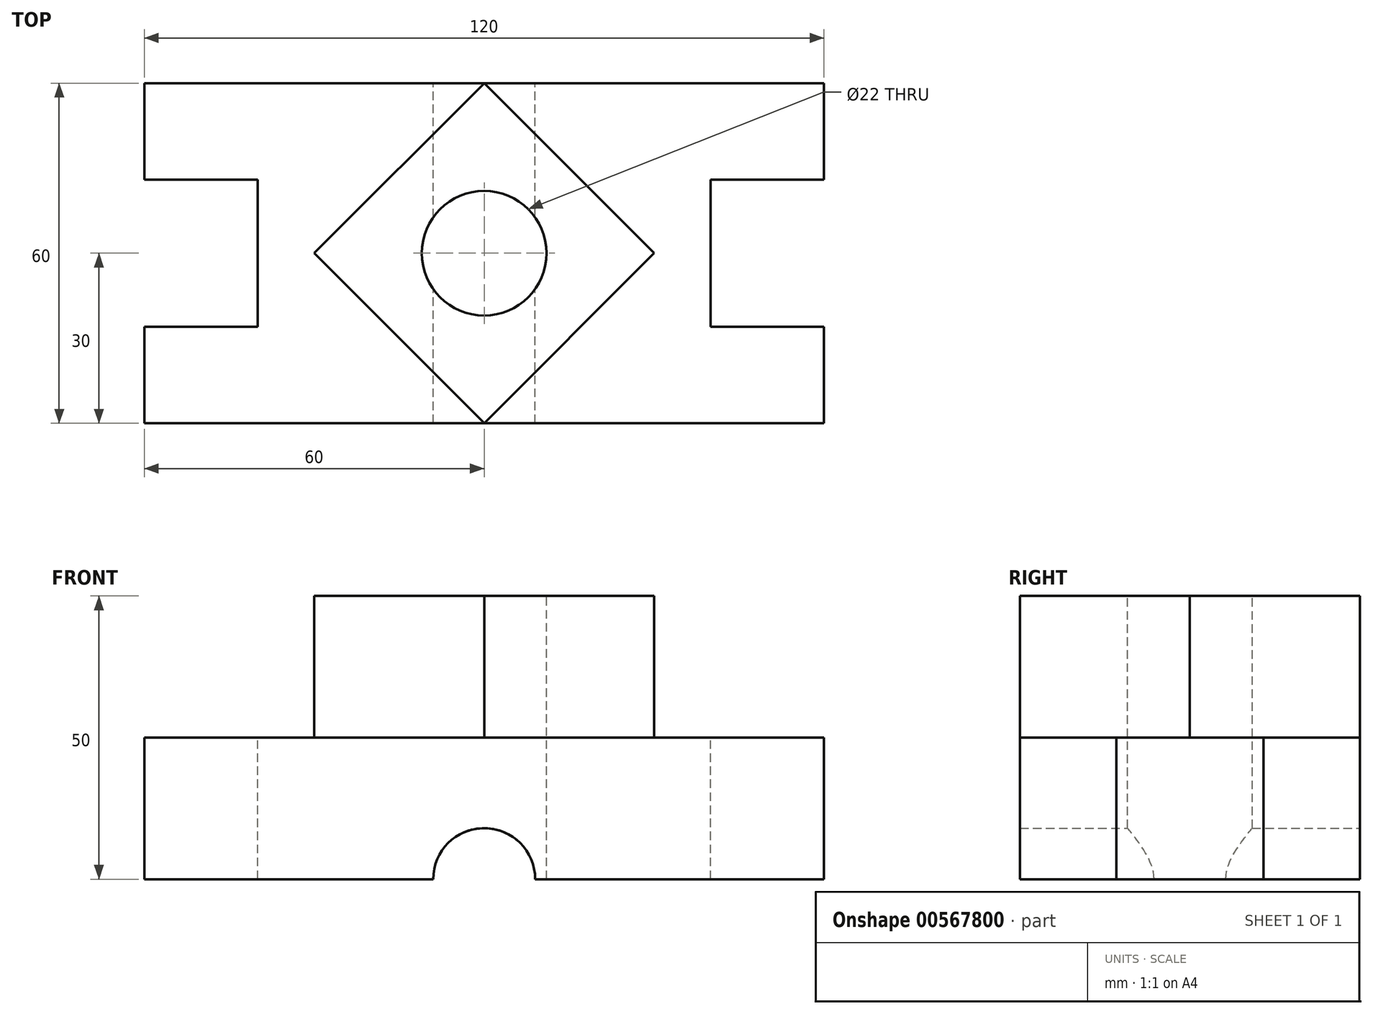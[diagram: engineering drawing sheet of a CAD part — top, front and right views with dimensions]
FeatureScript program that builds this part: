
annotation { "Feature Type Name" : "Feature", "Feature Type Description" : "" }
export const myFeature = defineFeature(function(context is Context, id is Id, definition is map)
    precondition{}
    {
        {
            var Q0;
            Q0=qCreatedBy(makeId("Front.planeOp"),FACE);
            var sketch = newSketch(context, id + "F0", { "sketchPlane" : qUnion([Q0])});
            skLineSegment(sketch, "E0.bottom", {"start": v(60, 12.5) * mm, "end": v(-60, 12.5) * mm});
            skLineSegment(sketch, "E0.top", {"start": v(60, -12.5) * mm, "end": v(9, -12.5) * mm});
            skLineSegment(sketch, "E0.left", {"start": v(60, 12.5) * mm, "end": v(60, -12.5) * mm});
            skLineSegment(sketch, "E0.right", {"start": v(-60, 12.5) * mm, "end": v(-60, -12.5) * mm});
            skArc(sketch, "E1", {"start": v(9, -12.5) * mm, "mid": v(0, -3.5) * mm, "end": v(-9, -12.5) * mm});
            skLineSegment(sketch, "E2.trimOffspring", {"start": v(-9, -12.5) * mm, "end": v(-60, -12.5) * mm});
            skSolve(sketch);
        }
        {
            var Q0;
            Q0=qSketchRegion(id+"F0",true);
            extrude(context, id + "F1", {"entities" : qUnion([Q0]), "depth" : 60 * mm, "offsetDistance" : 25 * mm});
        }
        {
            var Q0;
            Q0=makeQuery(id+"F1.opExtrude","SWEPT_FACE",FACE,{"disambiguationData":[OSD([sQuery(id+"F0.wireOp",EDGE,"E0.bottom")])]});
            var sketch = newSketch(context, id + "F2", { "sketchPlane" : qUnion([Q0])});
            skLineSegment(sketch, "E3", {"start": v(-60, -47.5) * mm, "end": v(-60, -60) * mm});
            skPoint(sketch, "E4.start.orphan", {"position": v(-34.64, -9) * mm});
            skLineSegment(sketch, "E5.bottom", {"start": v(-40, -17) * mm, "end": v(-60, -17) * mm});
            skLineSegment(sketch, "E5.top", {"start": v(-40, -43) * mm, "end": v(-60, -43) * mm});
            skLineSegment(sketch, "E5.left", {"start": v(-40, -17) * mm, "end": v(-40, -43) * mm});
            skPoint(sketch, "E5.middle", {"position": v(-60, -30) * mm});
            skPoint(sketch, "E6.orphan", {"position": v(-80, -43) * mm});
            skPoint(sketch, "E7.orphan", {"position": v(-80, -17) * mm});
            skPoint(sketch, "E8.orphan", {"position": v(-60, -35) * mm});
            skLineSegment(sketch, "E9.trimOffspring", {"start": v(-60, -35) * mm, "end": v(-60, -43) * mm});
            skPoint(sketch, "E10.start.orphan", {"position": v(-60, 0) * mm});
            skPoint(sketch, "E11.end.orphan", {"position": v(-34.64, -60) * mm});
            skPoint(sketch, "E12.orphan", {"position": v(-60, -47.5) * mm});
            skLineSegment(sketch, "E13", {"start": v(60, -43) * mm, "end": v(40, -43) * mm});
            skLineSegment(sketch, "E14", {"start": v(40, -43) * mm, "end": v(40, -17) * mm});
            skLineSegment(sketch, "E15", {"start": v(40, -17) * mm, "end": v(60, -17) * mm});
            skSolve(sketch);
        }
        {
            var Q0;
            Q0=qSketchRegion(id+"F2",true);
            var Q1;
            {var subQ1=sQuery(id+"F2.wireOp",EDGE,"E5.bottom");Q1=makeQuery(id+"F2.imprint","IMPRINT",FACE,{"disambiguationData":[TD([[makeQuery(id+"F2.imprint","IMPRINT",EDGE,{"derivedFrom":subQ1}),1.0]])]});}
            var Q2;
            {var subQ0=sQuery(id+"F2.wireOp",EDGE,"E13");Q2=makeQuery(id+"F2.imprint","IMPRINT",FACE,{"disambiguationData":[TD([[makeQuery(id+"F2.imprint","IMPRINT",EDGE,{"derivedFrom":subQ0}),-1.0]])]});}
            extrude(context, id + "F3", {"entities" : qUnion([Q0, Q1, Q2]), "operationType" : NewBodyOperationType.REMOVE, "endBound" : BoundingType.THROUGH_ALL, "oppositeDirection" : true, "depth" : 25 * mm, "offsetDistance" : 25 * mm});
        }
        {
            var Q0;
            Q0=makeQuery(id+"F1.opExtrude","SWEPT_FACE",FACE,{"disambiguationData":[OSD([sQuery(id+"F0.wireOp",EDGE,"E0.bottom")])]});
            var sketch = newSketch(context, id + "F4", { "sketchPlane" : qUnion([Q0])});
            skLineSegment(sketch, "E16", {"start": v(0, -60) * mm, "end": v(-30, -30) * mm});
            skPoint(sketch, "E16.endSnap0", {"position": v(-40, -30) * mm});
            skLineSegment(sketch, "E17", {"start": v(-30, -30) * mm, "end": v(0, 0) * mm});
            skLineSegment(sketch, "E18", {"start": v(0, 0) * mm, "end": v(30, -30) * mm});
            skPoint(sketch, "E18.endSnap0", {"position": v(40, -30) * mm});
            skLineSegment(sketch, "E19", {"start": v(30, -30) * mm, "end": v(0, -60) * mm});
            skSolve(sketch);
        }
        {
            var Q0;
            Q0=qSketchRegion(id+"F4",true);
            extrude(context, id + "F5", {"entities" : qUnion([Q0]), "operationType" : NewBodyOperationType.ADD, "depth" : 25 * mm, "offsetDistance" : 25 * mm});
        }
        {
            var Q0;
            Q0=makeQuery(id+"F5.opExtrude","CAP_FACE",FACE,{"disambiguationData":[OSD([sQuery(id+"F4.wireOp",EDGE,"E16"),sQuery(id+"F4.wireOp",EDGE,"E17"),sQuery(id+"F4.wireOp",EDGE,"E18"),sQuery(id+"F4.wireOp",EDGE,"E19")])],"isStart":false});
            var sketch = newSketch(context, id + "F6", { "sketchPlane" : qUnion([Q0])});
            skCircle(sketch, "E20", {"center": v(0, -30) * mm, "radius": 11 * mm});
            skSolve(sketch);
        }
        {
            var Q0;
            Q0=makeQuery(id+"F6.imprint","IMPRINT",FACE,{"disambiguationData":[TD([[makeQuery(id+"F6.imprint","IMPRINT",EDGE,{"derivedFrom":sQuery(id+"F6.wireOp",EDGE,"E20")}),1.0]])]});
            extrude(context, id + "F7", {"entities" : qUnion([Q0]), "operationType" : NewBodyOperationType.REMOVE, "oppositeDirection" : true, "depth" : 50 * mm, "offsetDistance" : 25 * mm});
        }
    });
